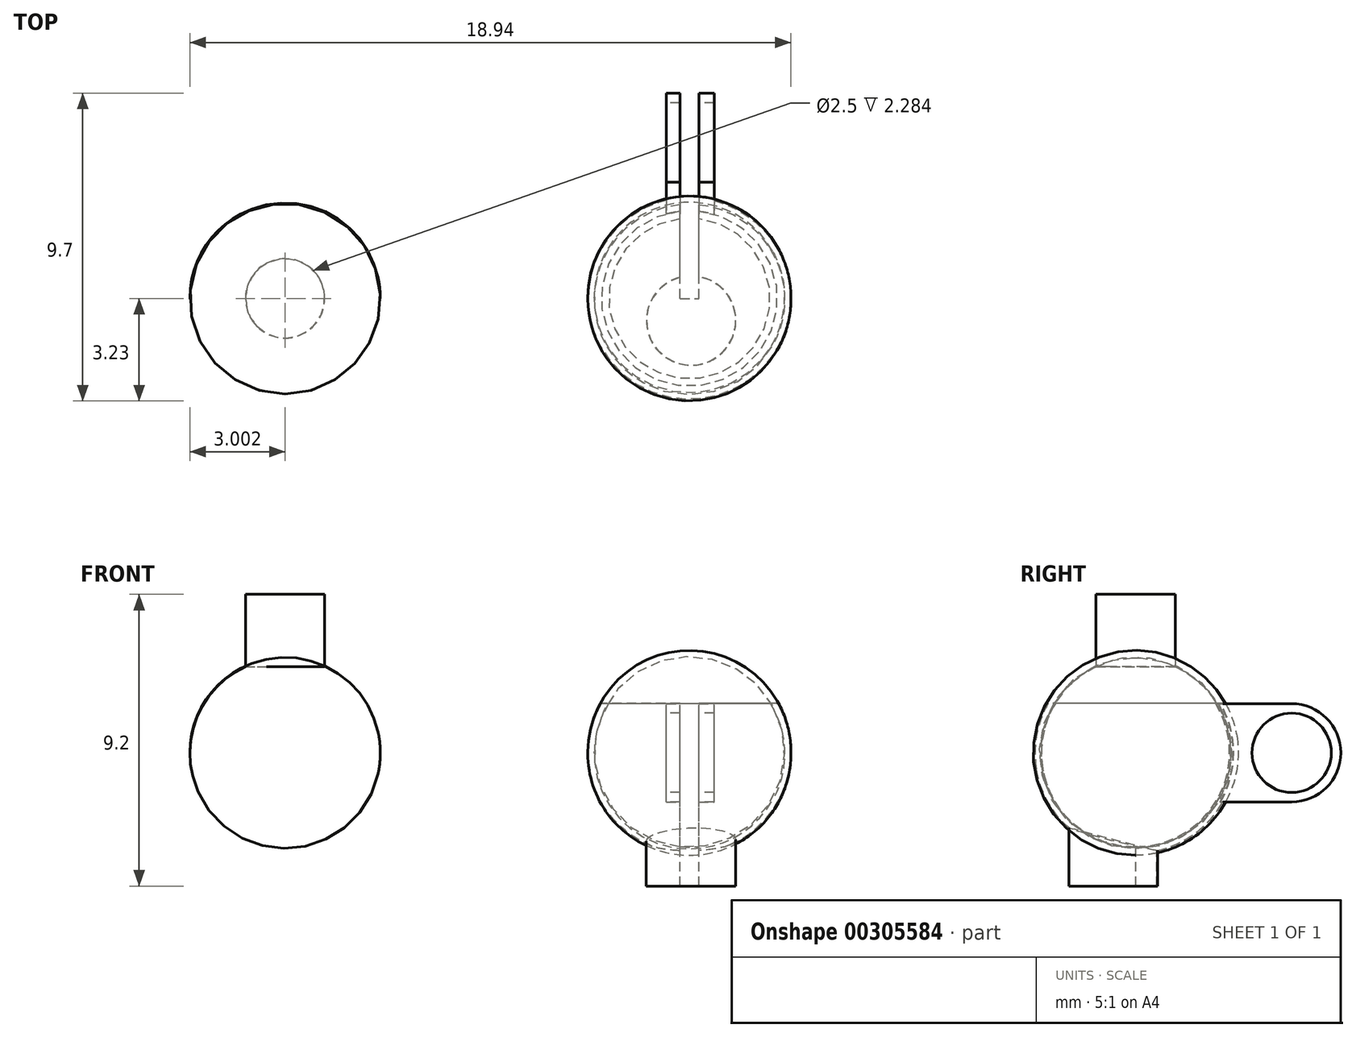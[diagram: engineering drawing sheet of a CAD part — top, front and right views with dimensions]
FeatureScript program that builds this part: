
annotation { "Feature Type Name" : "Feature", "Feature Type Description" : "" }
export const myFeature = defineFeature(function(context is Context, id is Id, definition is map)
    precondition{}
    {
        {
            var Q0;
            Q0=qCreatedBy(makeId("Front.planeOp"),FACE);
            var sketch = newSketch(context, id + "F0", { "sketchPlane" : qUnion([Q0])});
            skLineSegment(sketch, "E0", {"start": v(-53.27, 0) * mm, "end": v(-47.27, 0) * mm});
            skArc(sketch, "E1", {"start": v(-47.27, 0) * mm, "mid": v(-50.27, 2.99) * mm, "end": v(-53.27, 0) * mm});
            skSolve(sketch);
        }
        {
            var Q0;
            Q0 = qSketchRegion(id + "F0", true);
            var Q1;
            Q1=sQuery(id+"F0.wireOp",EDGE,"E0");
            revolve(context, id + "F1", {"entities" : qUnion([Q0]), "axis" : qUnion([Q1]), "revolveType" : RevolveType.FULL});
        }
        {
            var Q0;
            Q0=qCreatedBy(makeId("Top.planeOp"),FACE);
            var sketch = newSketch(context, id + "F2", { "sketchPlane" : qUnion([Q0])});
            skPoint(sketch, "E2.0", {"position": v(-50.27, 0) * mm});
            skCircle(sketch, "E3", {"center": v(-50.27, 0) * mm, "radius": 1.25 * mm});
            skSolve(sketch);
        }
        {
            var Q0;
            Q0=makeQuery(id+"F2.imprint","IMPRINT",FACE,{"disambiguationData":[TD([[makeQuery(id+"F2.imprint","IMPRINT",EDGE,{"derivedFrom":sQuery(id+"F2.wireOp",EDGE,"E3")}),1.0]])]});
            var Q1;
            Q1=sQuery(id+"F2.wireOp",EDGE,"E3");
            extrude(context, id + "F3", {"entities" : qUnion([Q0]), "operationType" : NewBodyOperationType.ADD, "surfaceEntities" : qUnion([Q1]), "depth" : 5 * mm});
        }
        {
            var Q0;
            Q0=qCreatedBy(makeId("Front.planeOp"),FACE);
            var sketch = newSketch(context, id + "F4", { "sketchPlane" : qUnion([Q0])});
            skLineSegment(sketch, "E4", {"start": v(-40.53, 0) * mm, "end": v(-34.53, 0) * mm});
            skArc(sketch, "E5", {"start": v(-34.53, 0) * mm, "mid": v(-37.53, 2.97) * mm, "end": v(-40.53, 0) * mm});
            skArc(sketch, "E6.0", {"start": v(-34.33, 0) * mm, "mid": v(-37.53, 3.17) * mm, "end": v(-40.73, 0) * mm});
            skLineSegment(sketch, "E7", {"start": v(-40.73, 0) * mm, "end": v(-34.33, 0) * mm});
            skSolve(sketch);
        }
        {
            var Q0;
            {var subQ4=sQuery(id+"F4.wireOp",EDGE,"E6.0");Q0=makeQuery(id+"F4.imprint","IMPRINT",FACE,{"disambiguationData":[TD([[makeQuery(id+"F4.imprint","IMPRINT",EDGE,{"derivedFrom":subQ4}),1.0]])]});}
            var Q1;
            Q1=sQuery(id+"F4.wireOp",EDGE,"E6.0");
            var Q2;
            Q2=sQuery(id+"F4.wireOp",EDGE,"E7");
            revolve(context, id + "F5", {"entities" : qUnion([Q0]), "surfaceEntities" : qUnion([Q1]), "axis" : qUnion([Q2]), "revolveType" : RevolveType.FULL});
        }
        {
            var Q0;
            Q0=qCreatedBy(makeId("Right.planeOp"),FACE);
            cPlane(context, id + "F6", {"entities" : qUnion([Q0]), "cplaneType" : CPlaneType.OFFSET, "offset" : 38.25 * mm, "oppositeDirection" : true, "width" : 150 * mm, "height" : 150 * mm});
        }
        {
            var Q0;
            Q0=qCreatedBy(id+"F6.planeOp",FACE);
            var sketch = newSketch(context, id + "F7", { "sketchPlane" : qUnion([Q0])});
            skLineSegment(sketch, "E8", {"start": v(0, 0) * mm, "end": v(7.17, 0) * mm, "construction": true});
            skCircle(sketch, "E9", {"center": v(4.92, 0) * mm, "radius": 1.55 * mm});
            skLineSegment(sketch, "E10", {"start": v(4.92, 2) * mm, "end": v(4.92, -1.79) * mm, "construction": true});
            skLineSegment(sketch, "E11", {"start": v(4.92, 1.55) * mm, "end": v(2.64, 1.55) * mm});
            skLineSegment(sketch, "E12", {"start": v(4.92, -1.55) * mm, "end": v(2.64, -1.55) * mm});
            skLineSegment(sketch, "E13", {"start": v(2.64, -1.55) * mm, "end": v(2.64, 1.55) * mm});
            skCircle(sketch, "E14.0", {"center": v(4.92, 0) * mm, "radius": 1.25 * mm});
            skSolve(sketch);
        }
        {
            var Q0;
            {var subQ0=sQuery(id+"F7.wireOp",EDGE,"E11");Q0=makeQuery(id+"F7.imprint","IMPRINT",FACE,{"disambiguationData":[TD([[makeQuery(id+"F7.imprint","IMPRINT",EDGE,{"derivedFrom":subQ0}),1.0]])]});}
            var Q1;
            Q1=makeQuery(id+"F7.imprint","IMPRINT",FACE,{"disambiguationData":[TD([[makeQuery(id+"F7.imprint","IMPRINT",EDGE,{"derivedFrom":sQuery(id+"F7.wireOp",EDGE,"E14.0")}),-1.0]])]});
            extrude(context, id + "F8", {"entities" : qUnion([Q0, Q1]), "operationType" : NewBodyOperationType.ADD, "depth" : 1.5 * mm});
        }
        {
            var Q0;
            Q0=qCreatedBy(makeId("Top.planeOp"),FACE);
            cPlane(context, id + "F9", {"entities" : qUnion([Q0]), "cplaneType" : CPlaneType.OFFSET, "offset" : 2.2 * mm, "oppositeDirection" : true, "width" : 150 * mm, "height" : 150 * mm});
        }
        {
            var Q0;
            Q0=qCreatedBy(id+"F9.planeOp",FACE);
            var sketch = newSketch(context, id + "F10", { "sketchPlane" : qUnion([Q0])});
            skCircle(sketch, "E15", {"center": v(-37.47, -0.7) * mm, "radius": 1.4 * mm});
            skSolve(sketch);
        }
        {
            var Q0;
            Q0 = qSketchRegion(id + "F10", true);
            extrude(context, id + "F11", {"entities" : qUnion([Q0]), "operationType" : NewBodyOperationType.ADD, "oppositeDirection" : true, "depth" : 2 * mm});
        }
        {
            var Q0;
            {var subQ0=sQuery(id+"F4.wireOp",EDGE,"E7");var subQ1=sQuery(id+"F4.wireOp",EDGE,"E5");var subQ2=makeQuery(id+"F4.imprint","INTERSECT",VERTEX,{"disambiguationData":[OD(0.0)],"derivedFrom":[subQ1,subQ0]});Q0=makeQuery(id+"F4.imprint","IMPRINT",FACE,{"disambiguationData":[TD([[makeQuery(id+"F4.imprint","IMPRINT",EDGE,{"disambiguationData":[TD([[subQ2,-1.0]])],"derivedFrom":subQ1}),1.0]])]});}
            var Q1;
            Q1=sQuery(id+"F4.wireOp",EDGE,"E5");
            var Q2;
            Q2=sQuery(id+"F4.wireOp",EDGE,"E7");
            revolve(context, id + "F12", {"operationType" : NewBodyOperationType.REMOVE, "entities" : qUnion([Q0]), "surfaceEntities" : qUnion([Q1]), "axis" : qUnion([Q2]), "revolveType" : RevolveType.FULL, "oppositeDirection" : true});
        }
        {
            var Q0;
            Q0=qCreatedBy(makeId("Top.planeOp"),FACE);
            cPlane(context, id + "F13", {"entities" : qUnion([Q0]), "cplaneType" : CPlaneType.OFFSET, "offset" : 1.56 * mm, "width" : 150 * mm, "height" : 150 * mm});
        }
        {
            var Q0;
            Q0=qCreatedBy(id+"F13.planeOp",FACE);
            var sketch = newSketch(context, id + "F14", { "sketchPlane" : qUnion([Q0])});
            skPoint(sketch, "E16.0", {"position": v(-37.53, 0) * mm});
            skLineSegment(sketch, "E17", {"start": v(-37.53, 5.45) * mm, "end": v(-37.53, -6.13) * mm, "construction": true});
            skLineSegment(sketch, "E18", {"start": v(-42.67, 0) * mm, "end": v(-32.98, 0) * mm, "construction": true});
            skLineSegment(sketch, "E19", {"start": v(-40.76, 0) * mm, "end": v(-40.76, -2.09) * mm, "construction": true});
            skLineSegment(sketch, "E20", {"start": v(-40.76, -2.09) * mm, "end": v(-40.76, 2.07) * mm, "construction": true});
            skLineSegment(sketch, "E21", {"start": v(-37.53, 6.75) * mm, "end": v(-39.7, 6.75) * mm, "construction": true});
            skLineSegment(sketch, "E22", {"start": v(-39.7, 6.75) * mm, "end": v(-35.66, 6.75) * mm, "construction": true});
            skLineSegment(sketch, "E23.bottom", {"start": v(-40.76, 6.75) * mm, "end": v(-34.3, 6.75) * mm});
            skLineSegment(sketch, "E23.top", {"start": v(-40.76, -3.17) * mm, "end": v(-34.3, -3.17) * mm});
            skLineSegment(sketch, "E23.left", {"start": v(-40.76, 6.75) * mm, "end": v(-40.76, -3.17) * mm});
            skLineSegment(sketch, "E23.right", {"start": v(-34.3, 6.75) * mm, "end": v(-34.3, -3.17) * mm});
            skLineSegment(sketch, "E24.bottom", {"start": v(-37.82, 0) * mm, "end": v(-37.23, 0) * mm});
            skLineSegment(sketch, "E24.top", {"start": v(-37.82, 6.75) * mm, "end": v(-37.23, 6.75) * mm});
            skLineSegment(sketch, "E24.left", {"start": v(-37.82, 0) * mm, "end": v(-37.82, 6.75) * mm});
            skLineSegment(sketch, "E24.right", {"start": v(-37.23, 0) * mm, "end": v(-37.23, 6.75) * mm});
            skSolve(sketch);
        }
        {
            var Q0;
            Q0=makeQuery(id+"F14.imprint","IMPRINT",FACE,{"disambiguationData":[TD([[makeQuery(id+"F14.imprint","IMPRINT",EDGE,{"derivedFrom":sQuery(id+"F14.wireOp",EDGE,"E24.bottom")}),1.0]])]});
            extrude(context, id + "F15", {"entities" : qUnion([Q0]), "operationType" : NewBodyOperationType.REMOVE, "oppositeDirection" : true, "depth" : 25 * mm});
        }
        {
            var Q0;
            Q0 = qSketchRegion(id + "F14", true);
            extrude(context, id + "F16", {"entities" : qUnion([Q0]), "operationType" : NewBodyOperationType.REMOVE, "depth" : 2 * mm});
        }
    });
